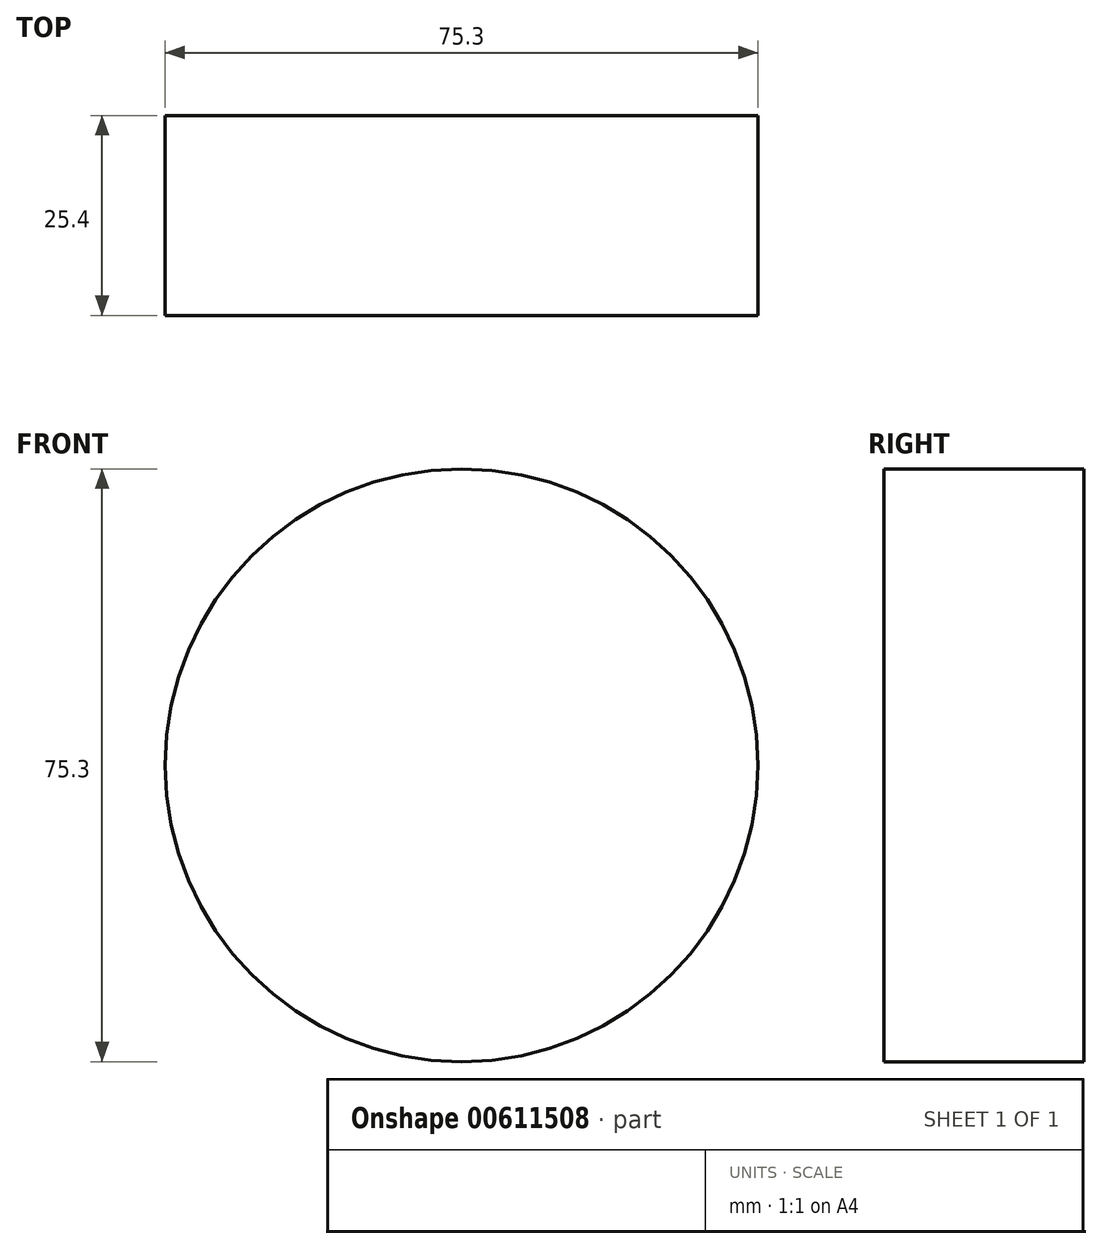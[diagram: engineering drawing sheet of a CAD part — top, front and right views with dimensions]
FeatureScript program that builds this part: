
annotation { "Feature Type Name" : "Feature", "Feature Type Description" : "" }
export const myFeature = defineFeature(function(context is Context, id is Id, definition is map)
    precondition{}
    {
        {
            var Q0;
            Q0=qCreatedBy(makeId("Front.planeOp"),FACE);
            var sketch = newSketch(context, id + "F0", { "sketchPlane" : qUnion([Q0])});
            skCircle(sketch, "E0", {"center": v(0, 0) * mm, "radius": 37.65 * mm});
            skPoint(sketch, "E1", {"position": v(4.76, 37.35) * mm});
            skPoint(sketch, "E2", {"position": v(37.65, 0) * mm});
            skPoint(sketch, "E3", {"position": v(0, -37.65) * mm});
            skPoint(sketch, "E4", {"position": v(-37.37, 4.6) * mm});
            skSolve(sketch);
        }
        {
            var Q0;
            Q0=sQuery(id+"F0.wireOp",EDGE,"E0");
            extrude(context, id + "F1", {"bodyType" : ToolBodyType.SURFACE, "surfaceEntities" : qUnion([Q0]), "depth" : 25.4 * mm, "offsetDistance" : 25.4 * mm});
        }
    });
